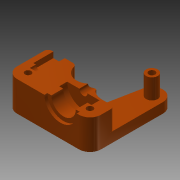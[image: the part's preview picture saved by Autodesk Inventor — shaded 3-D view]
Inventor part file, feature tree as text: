
AUTODESK INVENTOR PART (.ipt)
format: ipt  version: 2013 (Build 170138000, 138)  size: 232,448 bytes
history: native  units: mm
features: extrude x11, sketch x11, fillet x2
ambient origin geometry x8: Origin, YZ Plane, XZ Plane, XY Plane, X Axis, Y Axis, Z Axis, Center Point
bodies: Solid1 (feature_tree)
feature tree (24):
  extrude  "Extrusion1"  Depth=31.0mm
  extrude  "Extrusion2"  Depth=3.1mm
  extrude  "Extrusion3"  Depth=10.795mm
  extrude  "Extrusion4"  Depth=1.75mm
  extrude  "Extrusion5"  Depth=10.0mm TaperAngle=0.0deg
  extrude  "Extrusion6"  Depth=12.2mm
  extrude  "Extrusion7"  Depth=16.2mm
  extrude  "Extrusion8"  Depth=16.2mm
  extrude  "Extrusion9"  Depth=4.1mm
  fillet  "Fillet1"  Radius=1.0mm
  fillet  "Fillet2"  Radius=31.0mm
  extrude  "Extrusion10"  Depth=1.0mm TaperAngle=0.0deg
  extrude  "Extrusion11"  Depth=15.5mm
  sketch  "Sketch1"  dims[d0=13.5mm d2=31.0mm]
  sketch  "Sketch2"  dims[d3=42.0mm d4=3.1mm]
  sketch  "Sketch3"  dims[d5=15.0mm d6=0.0mm d7=10.795mm]
  sketch  "Sketch4"  dims[d9=8.5mm d11=1.75mm]
  sketch  "Sketch5"  dims[d12=2.0mm d13=10.0mm d14=0.0mm]
  sketch  "Sketch6"  dims[d15=6.2725mm d16=12.2mm]
  sketch  "Sketch7"  dims[d17=7.4mm d18=0.0mm d19=16.2mm]
  sketch  "Sketch8"  dims[d21=4.0mm d22=0.0mm d24=16.2mm]
  sketch  "Sketch9"  dims[d27=1.5mm d28=0.0mm d29=4.1mm d31=1.0mm d32=0.0mm d33=31.0mm]
  sketch  "Sketch10"  dims[d34=6.0mm d35=1.0mm d36=0.0mm]
  sketch  "Sketch11"  dims[d37=5.7mm d38=15.5mm d39=10.0mm d40=0.0mm d41=3.2mm d43=3.0mm d44=0.0mm d45=5.5mm d46=2.0mm d47=5.8mm d50=10.0mm d51=0.0mm d52=3.2mm d54=10.0mm d55=0.0mm]
